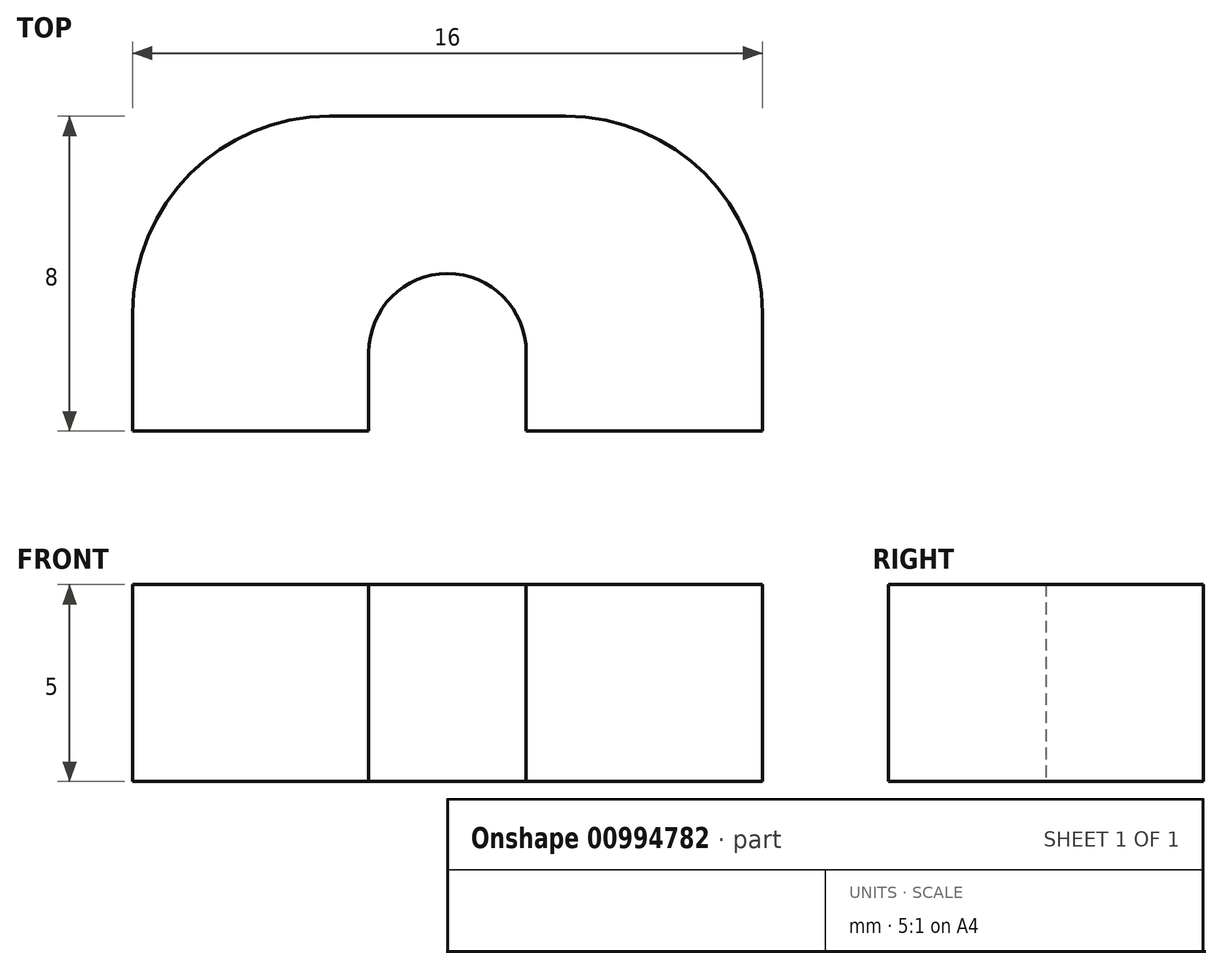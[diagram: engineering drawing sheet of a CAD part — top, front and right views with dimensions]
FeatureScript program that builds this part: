
annotation { "Feature Type Name" : "Feature", "Feature Type Description" : "" }
export const myFeature = defineFeature(function(context is Context, id is Id, definition is map)
    precondition{}
    {
        {
            var Q0;
            Q0=qCreatedBy(makeId("Top.planeOp"),FACE);
            var sketch = newSketch(context, id + "F0", { "sketchPlane" : qUnion([Q0])});
            skCircle(sketch, "E0", {"center": v(0, 0) * mm, "radius": 2 * mm});
            skLineSegment(sketch, "E1.bottom", {"start": v(8, -2) * mm, "end": v(-8, -2) * mm});
            skLineSegment(sketch, "E1.top", {"start": v(3, 6) * mm, "end": v(-3, 6) * mm});
            skLineSegment(sketch, "E1.left", {"start": v(8, -2) * mm, "end": v(8, 1) * mm});
            skLineSegment(sketch, "E1.right", {"start": v(-8, -2) * mm, "end": v(-8, 1) * mm});
            skPoint(sketch, "E1.middle", {"position": v(0, 2) * mm});
            skLineSegment(sketch, "E2", {"start": v(-2, 0) * mm, "end": v(-2, -2) * mm});
            skLineSegment(sketch, "E3", {"start": v(2, 0) * mm, "end": v(2, -2) * mm});
            skPoint(sketch, "E4.visualSharp", {"position": v(-8, 6) * mm});
            skArc(sketch, "E4.filletArc", {"start": v(-3, 6) * mm, "mid": v(-6.54, 4.54) * mm, "end": v(-8, 1) * mm});
            skPoint(sketch, "E5.visualSharp", {"position": v(8, 6) * mm});
            skArc(sketch, "E5.filletArc", {"start": v(8, 1) * mm, "mid": v(6.54, 4.54) * mm, "end": v(3, 6) * mm});
            skSolve(sketch);
        }
        {
            var Q0;
            Q0=makeQuery(id+"F0.imprint","IMPRINT",FACE,{"disambiguationData":[TD([[makeQuery(id+"F0.imprint","IMPRINT",EDGE,{"derivedFrom":sQuery(id+"F0.wireOp",EDGE,"E1.top")}),1.0]])]});
            extrude(context, id + "F1", {"entities" : qUnion([Q0]), "depth" : 5 * mm, "offsetDistance" : 25 * mm});
        }
    });
